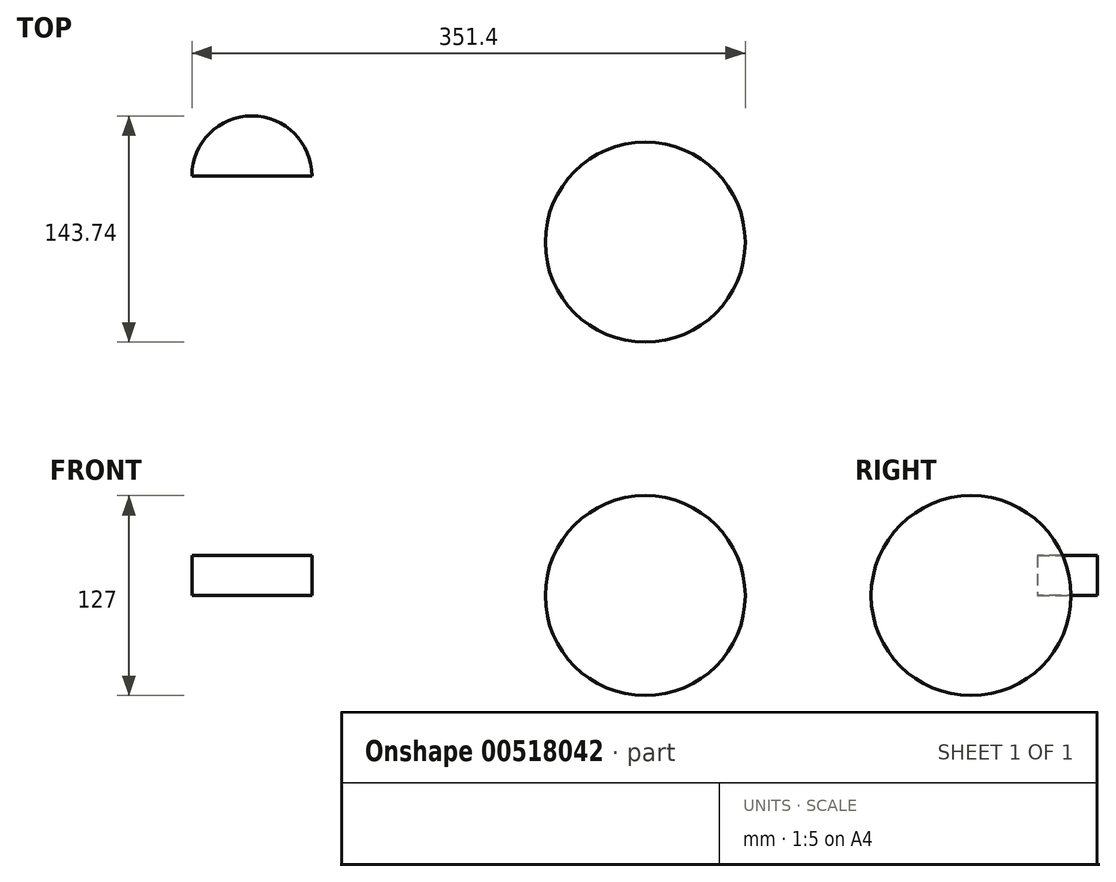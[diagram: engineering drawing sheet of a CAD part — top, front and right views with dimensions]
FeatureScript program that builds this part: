
annotation { "Feature Type Name" : "Feature", "Feature Type Description" : "" }
export const myFeature = defineFeature(function(context is Context, id is Id, definition is map)
    precondition{}
    {
        {
            var Q0;
            Q0=qCreatedBy(makeId("Top.planeOp"),FACE);
            var sketch = newSketch(context, id + "F0", { "sketchPlane" : qUnion([Q0])});
            skCircle(sketch, "E0", {"center": v(-44.84, 35.38) * mm, "radius": 38.1 * mm});
            skLineSegment(sketch, "E1.bottom", {"start": v(-82.94, 136.98) * mm, "end": v(-44.84, 136.98) * mm});
            skLineSegment(sketch, "E1.top", {"start": v(-82.94, 35.38) * mm, "end": v(-44.84, 35.38) * mm});
            skLineSegment(sketch, "E1.left", {"start": v(-82.94, 136.98) * mm, "end": v(-82.94, 35.38) * mm});
            skLineSegment(sketch, "E1.right", {"start": v(-44.84, 136.98) * mm, "end": v(-44.84, 35.38) * mm});
            skLineSegment(sketch, "E2.bottom", {"start": v(-44.84, 35.38) * mm, "end": v(183.76, 35.38) * mm});
            skLineSegment(sketch, "E2.top", {"start": v(-44.84, -2.47) * mm, "end": v(183.76, -2.47) * mm});
            skLineSegment(sketch, "E2.left", {"start": v(-44.84, 35.38) * mm, "end": v(-44.84, -2.47) * mm});
            skLineSegment(sketch, "E2.right", {"start": v(183.76, 35.38) * mm, "end": v(183.76, -2.47) * mm});
            skCircle(sketch, "E3.0", {"center": v(-44.84, 35.38) * mm, "radius": 44.45 * mm});
            skCircle(sketch, "E4", {"center": v(16.98, 89.05) * mm, "radius": 38.1 * mm});
            skSolve(sketch);
        }
        {
            var Q0;
            Q0=makeQuery(id+"F0.imprint","IMPRINT",FACE,{"disambiguationData":[TD([[makeQuery(id+"F0.imprint","IMPRINT",EDGE,{"derivedFrom":sQuery(id+"F0.wireOp",EDGE,"E0")}),1.0]])]});
            extrude(context, id + "F1", {"entities" : qUnion([Q0]), "depth" : 25.4 * mm});
        }
        {
            var Q0;
            Q0=qCreatedBy(makeId("Top.planeOp"),FACE);
            var sketch = newSketch(context, id + "F2", { "sketchPlane" : qUnion([Q0])});
            skArc(sketch, "E5", {"start": v(268.46, -6.76) * mm, "mid": v(204.96, 56.74) * mm, "end": v(141.46, -6.76) * mm});
            skLineSegment(sketch, "E6", {"start": v(141.46, -6.76) * mm, "end": v(268.46, -6.76) * mm});
            skSolve(sketch);
        }
        {
            var Q0;
            Q0=makeQuery(id+"F2.imprint","IMPRINT",FACE,{"disambiguationData":[TD([[makeQuery(id+"F2.imprint","IMPRINT",EDGE,{"derivedFrom":sQuery(id+"F2.wireOp",EDGE,"E5")}),1.0]])]});
            var Q1;
            Q1=sQuery(id+"F2.wireOp",EDGE,"E6");
            revolve(context, id + "F3", {"entities" : qUnion([Q0]), "axis" : qUnion([Q1]), "revolveType" : RevolveType.FULL});
        }
    });
